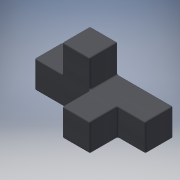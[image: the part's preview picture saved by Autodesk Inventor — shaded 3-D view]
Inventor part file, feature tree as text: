
AUTODESK INVENTOR PART (.ipt)
format: ipt  version: 2016 (Build 200138000, 138)  size: 177,664 bytes
history: native  units: in
note: dims shown in document units (in); Inventor stores cm internally (conversion verified against a paired STEP export)
features: plane x8, extrude x2, other x1, fillet x1, sketch x1
ambient origin geometry x8: Origin, YZ Plane, XZ Plane, XY Plane, X Axis, Y Axis, Z Axis, Center Point
bodies: Solid1 (feature_tree)
feature tree (13):
  other  "Cube Master.ipt"
  extrude  "Extrusion1"  Depth=0.3937in
  extrude  "Extrusion2"  Depth=0.0193in TaperAngle=0.0deg
  fillet  "Fillet1"  [1 undecoded]
  sketch  "Sketch1"  dims[d0=0.3937in d1=0.3937in d2=1.0in d3=0.0in d4=0.0in d5=0.0in d7=0.0193in d8=0.0193in]
  plane  "Work Plane1"
  plane  "Work Plane2"
  plane  "Work Plane3"
  plane  "Work Plane4"
  plane  "Work Plane5"
  plane  "Work Plane6"
  plane  "Work Plane7"
  plane  "Work Plane8"
note: 1 required parameter value undecoded (feature->parameter linkage not recoverable at this tier; creation-order binding heuristic only, values carry confidence <= 0.55)
